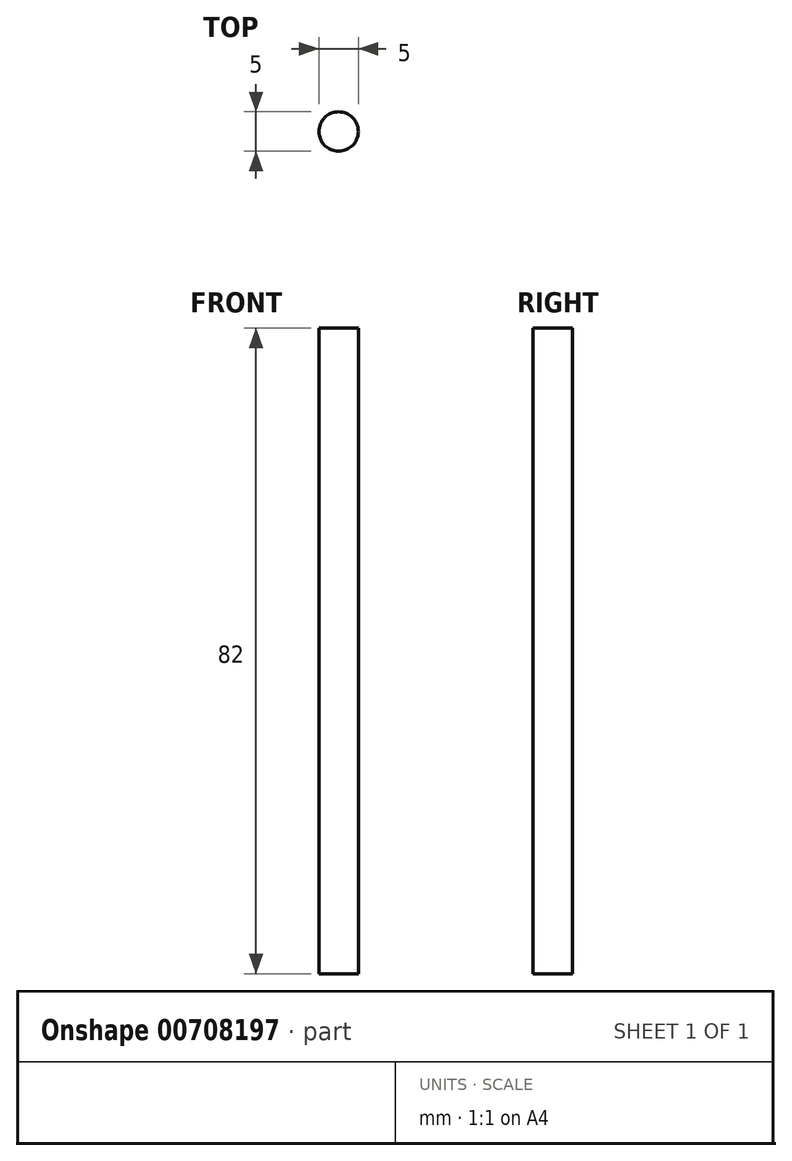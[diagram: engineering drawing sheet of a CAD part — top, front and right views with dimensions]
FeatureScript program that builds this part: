
annotation { "Feature Type Name" : "Feature", "Feature Type Description" : "" }
export const myFeature = defineFeature(function(context is Context, id is Id, definition is map)
    precondition{}
    {
        {
            var Q0;
            Q0=qCreatedBy(makeId("Top.planeOp"),FACE);
            var sketch = newSketch(context, id + "F0", { "sketchPlane" : qUnion([Q0])});
            skCircle(sketch, "E0", {"center": v(0, 0) * mm, "radius": 2.5 * mm});
            skSolve(sketch);
        }
        {
            var Q0;
            Q0=makeQuery(id+"F0.imprint","IMPRINT",FACE,{"disambiguationData":[TD([[makeQuery(id+"F0.imprint","IMPRINT",EDGE,{"derivedFrom":sQuery(id+"F0.wireOp",EDGE,"E0")}),1.0]])]});
            extrude(context, id + "F1", {"entities" : qUnion([Q0]), "depth" : 82 * mm, "offsetDistance" : 25 * mm});
        }
    });
